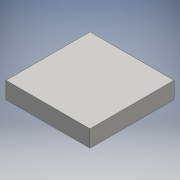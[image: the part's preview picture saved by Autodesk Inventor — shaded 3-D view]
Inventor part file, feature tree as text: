
AUTODESK INVENTOR PART (.ipt)
format: ipt  version: 2016 (Build 200138000, 138)  size: 85,504 bytes
history: native  units: mm
features: extrude x1, sketch x1
ambient origin geometry x8: Origin, YZ Plane, XZ Plane, XY Plane, X Axis, Y Axis, Z Axis, Center Point
bodies: Solid1 (feature_tree)
feature tree (2):
  extrude  "Extrusion1"  Depth=50.0mm
  sketch  "Sketch1"  dims[d0=50.0mm d1=50.0mm d2=25.0mm d3=25.0mm d4=10.0mm d5=0.0mm]
